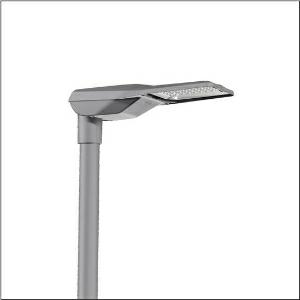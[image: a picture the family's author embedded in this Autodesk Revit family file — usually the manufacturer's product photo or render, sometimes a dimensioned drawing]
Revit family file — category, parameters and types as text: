
# Revit family: streetlight_sl_21_iq_mini___p0_8ab_5xe2r31g08gb_8bc5
name_source: partatom
category: Lighting Fixtures
units: mm (PartAtom-declared; Revit-internal decimal feet)

## family parameters
Cut with Voids When Loaded = No
Host = Face
Light Source = No
Part Type = Normal
Room Calculation Point = No
Round Connector Dimension = Use Diameter
Shared = No

## types (1)
- --- (1 x LED, 4930 lm, 37.1 W, 3000K)
    Apparent Load = 37 VA
    CIE Flux Codes = 36 71 98 100 100
    Color Rendering = 70
    Color Temperature = 3000K
    Default Elevation = 1800 mm
    Description = Streetlight SL 21 iQ mini, mast luminaire, primary light control with lens, of PMMA, primary optical cover: cover, of toughened safety glass, transparent, light distribution: P0.8aB, light emission: direct distribution, primary light characteristic: asymmetric, installation type: post-top, side-entry, LED, High Power LED, rated luminous flux: 4.930lm, luminous efficacy: 133lm/W, light colour: 730, colour temperature: 3000K, control gear: iQ Street-Remote, control: pre-setting: linear dimming characteristic, Street-Remote, Auto-Match, Temp-Guard, Lumen-Switch, Night-Set, Smart-Wire, Light-Fading, Desk-Remote (wireless, voltage-free reading and setting of iQ features in the workshop via application-optimized NFC function/RFID function), optimised constant luminous flux control (CLO 2.0), mains connection: 220..240V, AC, 50/60Hz, start of lifetime: 37W, end of service life: 39W, reduction: 18W, luminaire housing, of diecast aluminium, powder-coated, Siteco® metallic grey (DB 702S), corrosivity category C5 mid according to DIN EN ISO 12944, please order mast flange separately, inclination adjustable: 0°, 5°, 10°, 15°, sealing non-destructively replaceable, multi-level sealing system, length: 628mm, width: 235mm, height: 110mm, mast flange for spigot size: 42mm (side-entry): 5XC10008XM4, 60/48mm (side-entry/post-top): 5XC10108XM2, 76/60mm (side-entry/post-top): 5XC10108XM1, mounting height: 4..8m, protection rating (complete): IP66, insulation class (complete): insulation class II (safety insulation), certification: CE, ENEC, ENEC+, VDE, impact resistance: IK10, permissible operating ambient temperature for outdoor applications: -40..+50°C, standard-compliant lighting for roads and squares, packaging unit: 1 piece

Light Distribution: P0.8aB
    Height = 110 mm
    Lamp = 1 x LED
    Lamp Light Flux = 4930 lm
    Lamp Power = 37.1 W
    Lamp count = 1
    Length = 625 mm
    Luminous efficacy = 133 lm/W
    Manufacturer = Siteco
    ModVariant = No
    Model = 5XE2R31G08GB
    Number of Poles = 1
    OnlyDefault = Yes
    Power Factor = 1
    Product Name = Streetlight SL 21 iQ mini | P0.8aB
    Product group = mast luminaire | pylon top
    ProductGroupID = 6100
    Protection Class = Protection class II
    Protection Degree = IP 66
    RLX_Detail_Level = 1
    RLX_Emergency_Light_Flux = 0 lm
    RLX_Emergency_Type = 0
    RLX_Emergency_Type_DB = No
    RlxData = <blob elided: 91769 chars, md5=b5525b7f>
    Socket = socket
    Standby Power = 0 W
    System Light Flux = 4930 lm
    System Power = 37 W
    Type Comments = factory setting: luminous flux: 100 % | dim-lin: 254 | 385 mA
    Type Image = l_1003519.jpg
    URL = http://relux.com
    VarID = @adj_096045
    Voltage = 0 V
    Weight = 0.00 kg
    Width = 234 mm

## geometry (parser evidence)
native form markers: Blend x4, Sweep x14
no freeform markers — native parametric forms only
